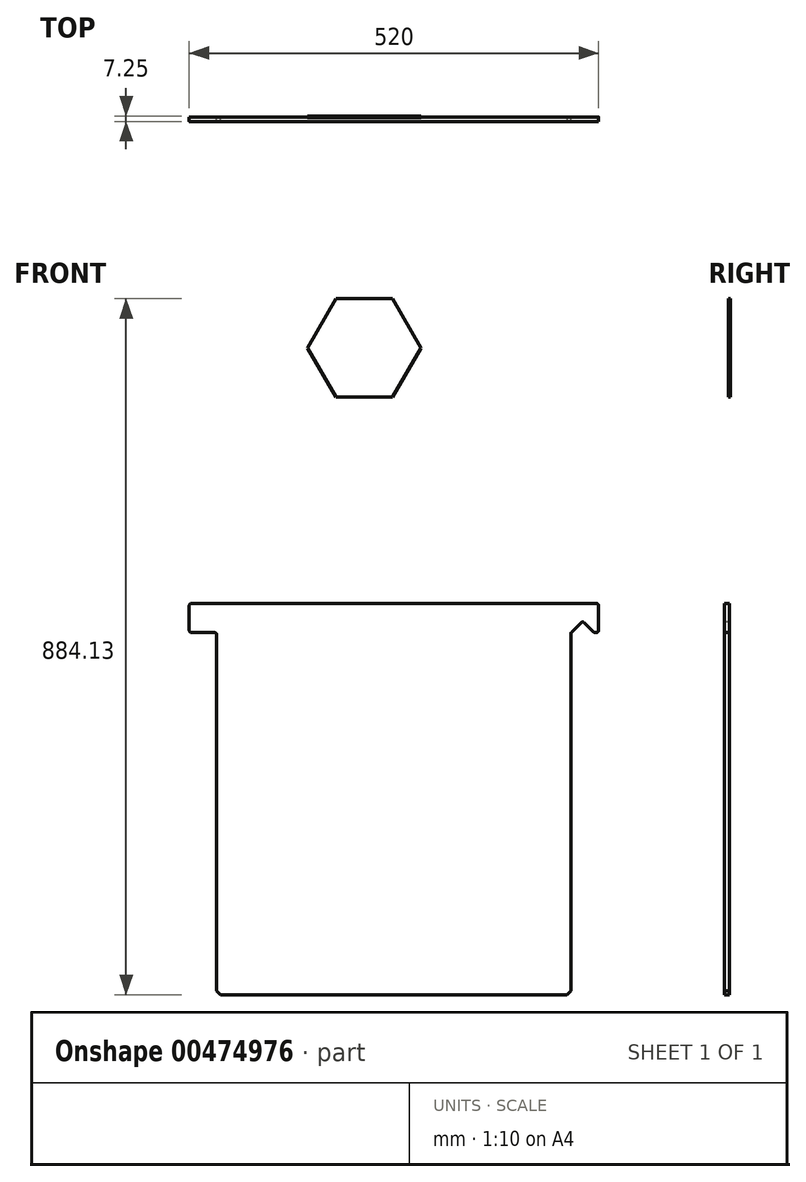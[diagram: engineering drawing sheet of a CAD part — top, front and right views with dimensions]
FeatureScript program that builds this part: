
annotation { "Feature Type Name" : "Feature", "Feature Type Description" : "" }
export const myFeature = defineFeature(function(context is Context, id is Id, definition is map)
    precondition{}
    {
        {
            var Q0;
            Q0=qCreatedBy(makeId("Front.planeOp"),FACE);
            var sketch = newSketch(context, id + "F0", { "sketchPlane" : qUnion([Q0])});
            skLineSegment(sketch, "E0", {"start": v(-288.64, 228.29) * mm, "end": v(231.36, 228.29) * mm});
            skLineSegment(sketch, "E1", {"start": v(231.36, 191.29) * mm, "end": v(225.51, 191.29) * mm});
            skLineSegment(sketch, "E2", {"start": v(225.51, 191.29) * mm, "end": v(211.18, 205.86) * mm});
            skLineSegment(sketch, "E3", {"start": v(211.18, 205.86) * mm, "end": v(196.36, 191.29) * mm});
            skLineSegment(sketch, "E4", {"start": v(196.36, 191.29) * mm, "end": v(196.36, -268.71) * mm});
            skLineSegment(sketch, "E5", {"start": v(196.36, -268.71) * mm, "end": v(-253.64, -268.71) * mm});
            skLineSegment(sketch, "E6", {"start": v(-253.64, -268.71) * mm, "end": v(-253.64, 191.29) * mm});
            skLineSegment(sketch, "E7", {"start": v(-253.64, 191.29) * mm, "end": v(-288.64, 191.29) * mm});
            skLineSegment(sketch, "E8", {"start": v(-288.64, 191.29) * mm, "end": v(-288.64, 228.29) * mm});
            skLineSegment(sketch, "E9", {"start": v(231.36, 228.29) * mm, "end": v(231.36, 191.29) * mm});
            skSolve(sketch);
        }
        {
            var Q0;
            Q0=makeQuery(id+"F0.imprint","IMPRINT",FACE,{"disambiguationData":[TD([[makeQuery(id+"F0.imprint","IMPRINT",EDGE,{"derivedFrom":sQuery(id+"F0.wireOp",EDGE,"E0")}),-1.0]])]});
            extrude(context, id + "F1", {"entities" : qUnion([Q0]), "depth" : 6 * mm, "offsetDistance" : 25 * mm});
        }
        {
            var Q0;
            Q0=qCreatedBy(makeId("Front.planeOp"),FACE);
            var sketch = newSketch(context, id + "F2", { "sketchPlane" : qUnion([Q0])});
            skCircle(sketch, "E10.cCircle", {"center": v(-66.35, 552.91) * mm, "radius": 62.5 * mm, "construction": true});
            skLineSegment(sketch, "E10.0", {"start": v(-30.26, 490.4) * mm, "end": v(-102.44, 490.4) * mm});
            skLineSegment(sketch, "E10.1", {"start": v(-102.44, 490.4) * mm, "end": v(-138.53, 552.91) * mm});
            skLineSegment(sketch, "E10.2", {"start": v(-138.53, 552.91) * mm, "end": v(-102.44, 615.42) * mm});
            skLineSegment(sketch, "E10.3", {"start": v(-102.44, 615.42) * mm, "end": v(-30.26, 615.42) * mm});
            skLineSegment(sketch, "E10.4", {"start": v(-30.26, 615.42) * mm, "end": v(5.83, 552.91) * mm});
            skLineSegment(sketch, "E10.5", {"start": v(5.83, 552.91) * mm, "end": v(-30.26, 490.4) * mm});
            skPoint(sketch, "E10.0.midPoint", {"position": v(-66.35, 490.4) * mm});
            skSolve(sketch);
        }
        {
            var Q0;
            Q0=makeQuery(id+"F2.imprint","IMPRINT",FACE,{"disambiguationData":[TD([[makeQuery(id+"F2.imprint","IMPRINT",EDGE,{"derivedFrom":sQuery(id+"F2.wireOp",EDGE,"E10.0")}),-1.0]])]});
            extrude(context, id + "F3", {"entities" : qUnion([Q0]), "endBound" : BoundingType.SYMMETRIC, "depth" : 2.5 * mm});
        }
        {
            var Q0;
            Q0=makeQuery(id+"F1.opExtrude","SWEPT_EDGE",EDGE,{"disambiguationData":[OSD([sQuery(id+"F0.wireOp",EDGE,"E4"),sQuery(id+"F0.wireOp",EDGE,"E5")])]});
            var Q1;
            Q1=makeQuery(id+"F1.opExtrude","SWEPT_EDGE",EDGE,{"disambiguationData":[OSD([sQuery(id+"F0.wireOp",EDGE,"E5"),sQuery(id+"F0.wireOp",EDGE,"E6")])]});
            chamfer(context, id + "F4", {"entities" : qUnion([Q0, Q1]), "width" : 5 * mm, "tangentPropagation" : true});
        }
        {
            var Q0;
            Q0=makeQuery(id+"F1.opExtrude","SWEPT_EDGE",EDGE,{"disambiguationData":[OSD([sQuery(id+"F0.wireOp",EDGE,"E7"),sQuery(id+"F0.wireOp",EDGE,"E8")])]});
            fillet(context, id + "F5", {"entities" : qUnion([Q0]), "radius" : 3 * mm, "tangentPropagation" : true, "allowEdgeOverflow" : false});
        }
        {
            var Q0;
            Q0=makeQuery(id+"F1.opExtrude","SWEPT_EDGE",EDGE,{"disambiguationData":[OSD([sQuery(id+"F0.wireOp",EDGE,"E0"),sQuery(id+"F0.wireOp",EDGE,"E8")])]});
            fillet(context, id + "F6", {"entities" : qUnion([Q0]), "radius" : 3 * mm, "tangentPropagation" : true, "allowEdgeOverflow" : false});
        }
        {
            var Q0;
            Q0=makeQuery(id+"F1.opExtrude","SWEPT_EDGE",EDGE,{"disambiguationData":[OSD([sQuery(id+"F0.wireOp",EDGE,"E0"),sQuery(id+"F0.wireOp",EDGE,"E9")])]});
            fillet(context, id + "F7", {"entities" : qUnion([Q0]), "radius" : 3 * mm, "tangentPropagation" : true, "allowEdgeOverflow" : false});
        }
        {
            var Q0;
            Q0=makeQuery(id+"F1.opExtrude","SWEPT_EDGE",EDGE,{"disambiguationData":[OSD([sQuery(id+"F0.wireOp",EDGE,"E3"),sQuery(id+"F0.wireOp",EDGE,"E4")])]});
            fillet(context, id + "F8", {"entities" : qUnion([Q0]), "radius" : 3 * mm, "tangentPropagation" : true, "allowEdgeOverflow" : false});
        }
        {
            var Q0;
            Q0=makeQuery(id+"F1.opExtrude","SWEPT_EDGE",EDGE,{"disambiguationData":[OSD([sQuery(id+"F0.wireOp",EDGE,"E1"),sQuery(id+"F0.wireOp",EDGE,"E9")])]});
            fillet(context, id + "F9", {"entities" : qUnion([Q0]), "radius" : 3 * mm, "tangentPropagation" : true, "allowEdgeOverflow" : false});
        }
        {
            var Q0;
            Q0=makeQuery(id+"F1.opExtrude","SWEPT_EDGE",EDGE,{"disambiguationData":[OSD([sQuery(id+"F0.wireOp",EDGE,"E1"),sQuery(id+"F0.wireOp",EDGE,"E2")])]});
            fillet(context, id + "F10", {"entities" : qUnion([Q0]), "radius" : 3 * mm, "tangentPropagation" : true, "allowEdgeOverflow" : false});
        }
        {
            var Q0;
            Q0=makeQuery(id+"F1.opExtrude","SWEPT_EDGE",EDGE,{"disambiguationData":[OSD([sQuery(id+"F0.wireOp",EDGE,"E2"),sQuery(id+"F0.wireOp",EDGE,"E3")])]});
            fillet(context, id + "F11", {"entities" : qUnion([Q0]), "radius" : 3 * mm, "tangentPropagation" : true, "allowEdgeOverflow" : false});
        }
        {
            var Q0;
            Q0=makeQuery(id+"F1.opExtrude","SWEPT_EDGE",EDGE,{"disambiguationData":[OSD([sQuery(id+"F0.wireOp",EDGE,"E6"),sQuery(id+"F0.wireOp",EDGE,"E7")])]});
            fillet(context, id + "F12", {"entities" : qUnion([Q0]), "radius" : 3 * mm, "tangentPropagation" : true, "allowEdgeOverflow" : false});
        }
    });
